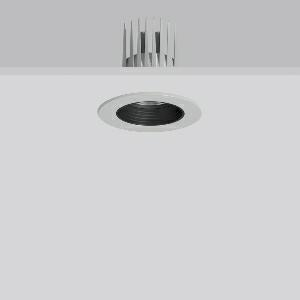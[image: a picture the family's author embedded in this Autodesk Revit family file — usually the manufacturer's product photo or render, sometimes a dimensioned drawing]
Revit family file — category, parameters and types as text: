
# Revit family: heledon_mini_e_901753_004_3_8c50
name_source: partatom
category: Lighting Fixtures
units: mm (PartAtom-declared; Revit-internal decimal feet)

## family parameters
Cut with Voids When Loaded = No
Host = Face
Light Source = No
Part Type = Normal
Room Calculation Point = No
Round Connector Dimension = Use Diameter
Shared = No

## types (1)
- HELEDON mini E (1 x LED Modul 935, 2900 lm, 3500)
    Apparent Load = 29 VA
    Approval mark = CE
    CIE Flux Codes = 98 100 100 100 100
    Color Rendering = 92
    Color Temperature = 3500
    Default Elevation = 1800 mm
    Description = Series: HELEDON mini
Round recessed downlight. Housing: die-cast aluminium, powder-coated. Black plastic ring and recessed LED to prevent glare from the side. Optical assembly with lens made of plastic (polycarbonate) for the best homogeneous light distribution - can be changed without tools. Best colour rendering index Ra>90. Suitable for Recessed ceiling mounting. Installation without tools thanks to spring fastening system. Including separate LED converter with connecting cable 600 mm.High quality converter without flickering and stroboscopic effect. Through-wiring box (5 pole) available as accessory. The following accessories can be mounted without use of tools: interchangeable lenses, decorative glasses, honeycomb louvre, clear and frosted diffusers, white interchangeable plastic ring. 
Colour: silver
Diameter: 124 mm
Height: 3 mm
Cut-out diameter: 114 mm
Recess height: 170 mm
Luminaire: recess height: 120 mm
Lamp: LED
Socket: without socket
Colour temperature: 3500K
Colour rendering index (CRI): 92
System power: 29 W
Rated luminous flux: 2900 lm
Luminous efficiency: 100 lm/W
Control gear: Regulated power supply
Protection class: II
Type of protection: IP 20
    Height = 0 mm  [stored 0 ft]
    Lamp = 1 x LED Modul 935
    Lamp Light Flux = 2900 lm
    Lamp count = 1
    Length = 124 mm  [stored 0.406824 ft]
    Lifetime = 50000 h
    Luminous efficacy = 100 lm/W
    Manufacturer = RZB
    ModVariant = No
    Model = 901753.004.3
    Mounting Place = Ceiling
    Mounting Type = Recessed
    Number of Poles = 1
    OnlyDefault = Yes
    Power Factor = 1
    Product Name = HELEDON mini E
    Product group = Recessed downlights
    ProductGroupID = 402
    Protection Class = Protection class II
    Protection Degree = IP 20
    RLX_Detail_Level = 1
    RLX_Emergency_Light_Flux = 0 lm
    RLX_Emergency_Type = 0
    RLX_Emergency_Type_DB = No
    RlxData = <blob elided: 127501 chars, md5=38550c36>
    Socket = socket
    Standby Power = 0 W
    System Light Flux = 2900 lm
    System Power = 29 W
    Type Comments = Product without accessories
    Type Image = 901656.004.jpg
    URL = http://relux.com
    VarID = ---
    Voltage = 230 V
    Voltage Range = 220-240 V
    Weight = 0.00 kg
    Width = 0 mm  [stored 0 ft]

note: [stored X ft] marks values corroborated as IEEE doubles in the binary element streams (Revit-internal decimal feet)

## geometry (parser evidence)
native form markers: Blend x4, Sweep x11
no freeform markers — native parametric forms only
